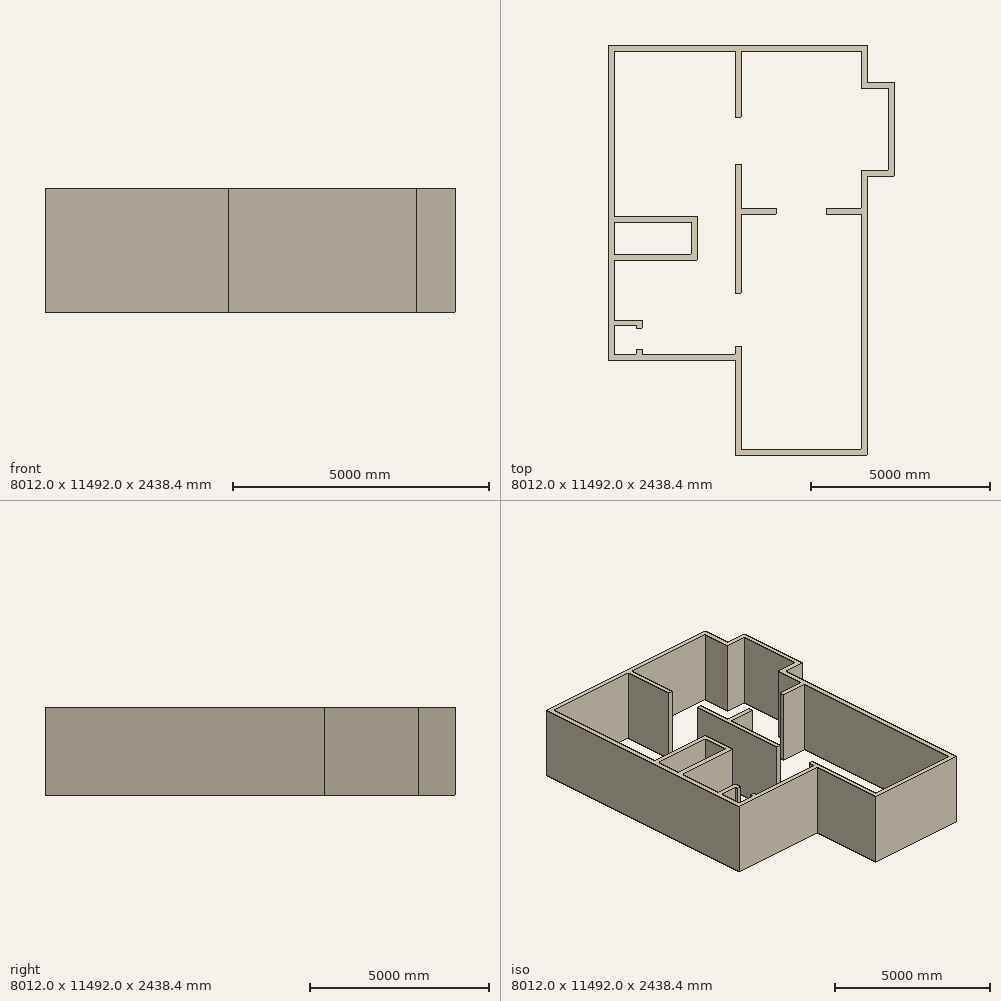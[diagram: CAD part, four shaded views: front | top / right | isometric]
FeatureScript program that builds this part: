
annotation { "Feature Type Name" : "Feature", "Feature Type Description" : "" }
export const myFeature = defineFeature(function(context is Context, id is Id, definition is map)
    precondition{}
    {
        {
            var Q0;
            Q0=qCreatedBy(makeId("Top.planeOp"),FACE);
            var sketch = newSketch(context, id + "F0", { "sketchPlane" : qUnion([Q0])});
            skLineSegment(sketch, "E0.bottom", {"start": v(-3883.24, 4955.77) * mm, "end": v(3366.73, 4955.77) * mm});
            skLineSegment(sketch, "E1.bottom", {"start": v(3202.14, 4791.17) * mm, "end": v(-150.66, 4791.17) * mm});
            skLineSegment(sketch, "E2.top", {"start": v(3202.14, -6371.6) * mm, "end": v(-150.66, -6371.6) * mm});
            skLineSegment(sketch, "E2.left", {"start": v(3202.14, 232.38) * mm, "end": v(3202.14, -6371.6) * mm});
            skLineSegment(sketch, "E3.bottom", {"start": v(-3718.65, 4791.17) * mm, "end": v(-315.25, 4791.17) * mm});
            skLineSegment(sketch, "E3.left", {"start": v(-3718.65, 4791.17) * mm, "end": v(-3718.65, 164.6) * mm});
            skLineSegment(sketch, "E4.bottom", {"start": v(-3718.65, 0) * mm, "end": v(-1561.38, 0) * mm});
            skLineSegment(sketch, "E4.top", {"start": v(-3718.65, -914.4) * mm, "end": v(-1561.38, -914.4) * mm});
            skLineSegment(sketch, "E4.left", {"start": v(-3718.65, 0) * mm, "end": v(-3718.65, -914.4) * mm});
            skLineSegment(sketch, "E4.right", {"start": v(-1561.38, 0) * mm, "end": v(-1561.38, -914.4) * mm});
            skLineSegment(sketch, "E5.bottom", {"start": v(-2931.45, -2739.84) * mm, "end": v(-3718.65, -2739.84) * mm});
            skLineSegment(sketch, "E6", {"start": v(-150.66, -6371.6) * mm, "end": v(-150.66, -3476) * mm});
            skLineSegment(sketch, "E7", {"start": v(-150.66, -3476) * mm, "end": v(-315.25, -3476) * mm});
            skLineSegment(sketch, "E8", {"start": v(-315.25, -3476) * mm, "end": v(-315.25, -3695.1) * mm});
            skLineSegment(sketch, "E9", {"start": v(-315.25, 1626.64) * mm, "end": v(-315.25, -2002.82) * mm});
            skLineSegment(sketch, "E10", {"start": v(-315.25, -2002.82) * mm, "end": v(-150.66, -2002.82) * mm});
            skLineSegment(sketch, "E11", {"start": v(-150.66, -2002.82) * mm, "end": v(-150.66, 232.38) * mm});
            skLineSegment(sketch, "E12", {"start": v(-150.66, 232.38) * mm, "end": v(814.52, 232.38) * mm});
            skLineSegment(sketch, "E13", {"start": v(814.52, 232.38) * mm, "end": v(814.52, 396.97) * mm});
            skLineSegment(sketch, "E14", {"start": v(814.52, 396.97) * mm, "end": v(-150.66, 396.97) * mm});
            skLineSegment(sketch, "E15", {"start": v(3202.14, 232.38) * mm, "end": v(2236.94, 232.38) * mm});
            skLineSegment(sketch, "E16", {"start": v(2236.94, 232.38) * mm, "end": v(2236.94, 396.97) * mm});
            skLineSegment(sketch, "E17", {"start": v(2236.94, 396.97) * mm, "end": v(3202.14, 396.97) * mm});
            skLineSegment(sketch, "E18", {"start": v(-3718.65, -1079) * mm, "end": v(-1400.46, -1079) * mm});
            skLineSegment(sketch, "E19", {"start": v(-1400.46, -1079) * mm, "end": v(-1400.46, 164.6) * mm});
            skLineSegment(sketch, "E20", {"start": v(-1400.46, 164.6) * mm, "end": v(-3718.65, 164.6) * mm});
            skLineSegment(sketch, "E21", {"start": v(-315.25, 4791.17) * mm, "end": v(-315.25, 2936.7) * mm});
            skLineSegment(sketch, "E22", {"start": v(-315.25, 2936.7) * mm, "end": v(-150.66, 2936.7) * mm});
            skLineSegment(sketch, "E23", {"start": v(-150.66, 2936.7) * mm, "end": v(-150.66, 4791.17) * mm});
            skLineSegment(sketch, "E24", {"start": v(-315.25, 1626.64) * mm, "end": v(-150.66, 1626.64) * mm});
            skLineSegment(sketch, "E25", {"start": v(-150.66, 1626.64) * mm, "end": v(-150.66, 396.97) * mm});
            skLineSegment(sketch, "E26", {"start": v(-315.25, -3859.68) * mm, "end": v(-315.25, -6536.19) * mm});
            skLineSegment(sketch, "E27", {"start": v(-315.25, -6536.19) * mm, "end": v(3366.73, -6536.19) * mm});
            skLineSegment(sketch, "E28", {"start": v(-3883.24, 4955.77) * mm, "end": v(-3883.24, -3859.68) * mm});
            skLineSegment(sketch, "E29", {"start": v(-3883.24, -3859.68) * mm, "end": v(-315.25, -3859.68) * mm});
            skLineSegment(sketch, "E30", {"start": v(-3718.65, -2904.43) * mm, "end": v(-3096.04, -2904.43) * mm});
            skLineSegment(sketch, "E31", {"start": v(-3096.04, -2904.43) * mm, "end": v(-3096.04, -2977.72) * mm});
            skLineSegment(sketch, "E32", {"start": v(-3096.04, -2977.72) * mm, "end": v(-2931.45, -2977.72) * mm});
            skLineSegment(sketch, "E33", {"start": v(-2931.45, -2977.72) * mm, "end": v(-2931.45, -2739.84) * mm});
            skLineSegment(sketch, "E34", {"start": v(-3096.04, -3695.1) * mm, "end": v(-3096.04, -3578.94) * mm});
            skLineSegment(sketch, "E35", {"start": v(-3096.04, -3578.94) * mm, "end": v(-2931.45, -3578.94) * mm});
            skLineSegment(sketch, "E36", {"start": v(-2931.45, -3578.94) * mm, "end": v(-2931.45, -3695.1) * mm});
            skLineSegment(sketch, "E37", {"start": v(-3718.65, -1079) * mm, "end": v(-3718.65, -2739.84) * mm});
            skLineSegment(sketch, "E38", {"start": v(-3718.65, -2904.43) * mm, "end": v(-3718.65, -3695.1) * mm});
            skLineSegment(sketch, "E39", {"start": v(-3096.04, -3695.1) * mm, "end": v(-3718.65, -3695.1) * mm});
            skLineSegment(sketch, "E40", {"start": v(-2931.45, -3695.1) * mm, "end": v(-315.25, -3695.1) * mm});
            skLineSegment(sketch, "E41", {"start": v(3366.73, 4955.77) * mm, "end": v(3366.73, 3914.37) * mm});
            skLineSegment(sketch, "E42", {"start": v(3366.73, 3914.37) * mm, "end": v(4128.73, 3914.37) * mm});
            skLineSegment(sketch, "E43", {"start": v(4128.73, 3914.37) * mm, "end": v(4128.73, 1273.78) * mm});
            skLineSegment(sketch, "E44", {"start": v(4128.73, 1273.78) * mm, "end": v(3366.73, 1273.78) * mm});
            skLineSegment(sketch, "E45", {"start": v(3366.73, 1273.78) * mm, "end": v(3366.73, -6536.19) * mm});
            skLineSegment(sketch, "E46", {"start": v(3202.14, 4791.17) * mm, "end": v(3202.14, 3749.77) * mm});
            skLineSegment(sketch, "E47", {"start": v(3202.14, 3749.77) * mm, "end": v(3964.14, 3749.77) * mm});
            skLineSegment(sketch, "E48", {"start": v(3964.14, 3749.77) * mm, "end": v(3964.14, 1438.37) * mm});
            skLineSegment(sketch, "E49", {"start": v(3964.14, 1438.37) * mm, "end": v(3202.14, 1438.37) * mm});
            skLineSegment(sketch, "E50", {"start": v(3202.14, 1438.37) * mm, "end": v(3202.14, 396.97) * mm});
            skSolve(sketch);
        }
        {
            var Q0;
            Q0=makeQuery(id+"F0.imprint","IMPRINT",FACE,{"disambiguationData":[TD([[makeQuery(id+"F0.imprint","IMPRINT",EDGE,{"derivedFrom":sQuery(id+"F0.wireOp",EDGE,"E0.bottom")}),-1.0]])]});
            var Q1;
            Q1=makeQuery(id+"F0.imprint","IMPRINT",FACE,{"disambiguationData":[TD([[makeQuery(id+"F0.imprint","IMPRINT",EDGE,{"derivedFrom":sQuery(id+"F0.wireOp",EDGE,"E9")}),1.0]])]});
            extrude(context, id + "F1", {"entities" : qUnion([Q0, Q1]), "depth" : 2438.4 * mm});
        }
    });
